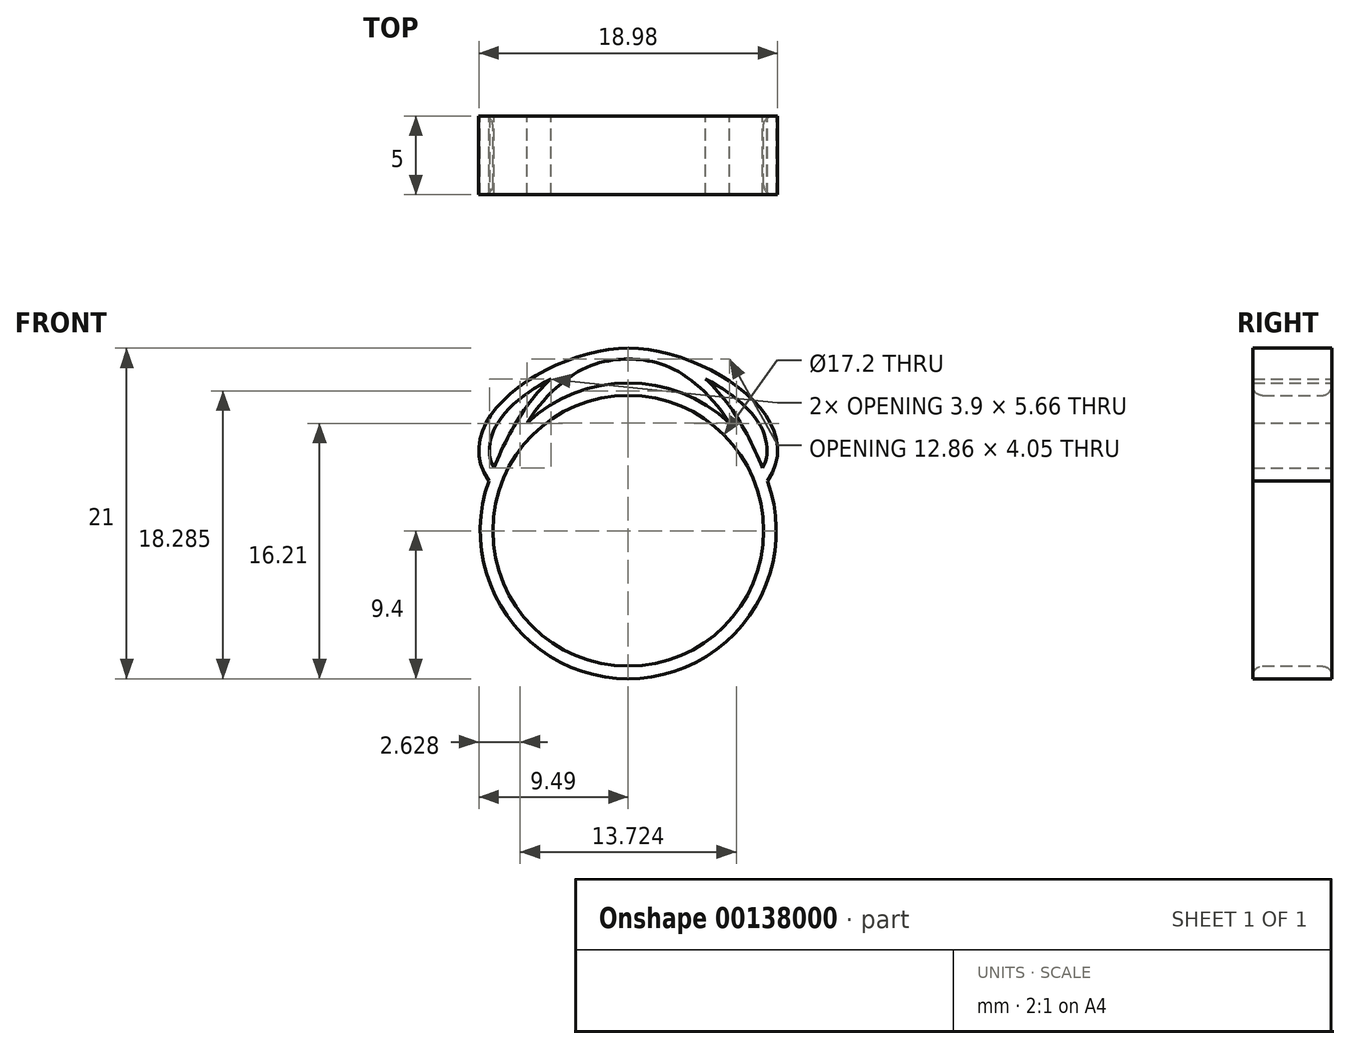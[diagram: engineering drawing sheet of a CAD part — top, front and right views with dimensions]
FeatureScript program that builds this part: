
annotation { "Feature Type Name" : "Feature", "Feature Type Description" : "" }
export const myFeature = defineFeature(function(context is Context, id is Id, definition is map)
    precondition{}
    {
        {
            var Q0;
            Q0=qCreatedBy(makeId("Front.planeOp"),FACE);
            var sketch = newSketch(context, id + "F0", { "sketchPlane" : qUnion([Q0])});
            skCircle(sketch, "E0", {"center": v(0, 0) * mm, "radius": 8.6 * mm});
            skCircle(sketch, "E1", {"center": v(0, 0) * mm, "radius": 9.4 * mm});
            skSolve(sketch);
        }
        {
            var Q0;
            Q0 = qSketchRegion(id + "F0", true);
            extrude(context, id + "F1", {"entities" : qUnion([Q0]), "depth" : 5 * mm});
        }
        {
            var Q0;
            Q0=qCreatedBy(makeId("Front.planeOp"),FACE);
            var sketch = newSketch(context, id + "F2", { "sketchPlane" : qUnion([Q0])});
            skLineSegment(sketch, "E2", {"start": v(-9.3, 3.17) * mm, "end": v(10.44, 3.17) * mm, "construction": true});
            skCircle(sketch, "E3.0", {"center": v(0, 0) * mm, "radius": 9.4 * mm, "construction": true});
            skFitSpline(sketch, "E4", {"points": [v(-8.85, 3.17) * mm, v(0, 11.6) * mm, v(8.85, 3.17) * mm], "startDerivative": vector(9, 24.34) * mm, "endDerivative": vector(-16.73, -24.34) * mm});
            skLineSegment(sketch, "E5", {"start": v(0, 3.17) * mm, "end": v(0, 13.95) * mm, "construction": true});
            skFitSpline(sketch, "E6.MirrorCS", {"points": [v(8.85, 3.17) * mm, v(0, 11.6) * mm, v(-8.85, 3.17) * mm], "startDerivative": vector(-9, 24.34) * mm, "endDerivative": vector(16.73, -24.34) * mm});
            skFitSpline(sketch, "E7.0", {"points": [v(8.2, 2.93) * mm, v(7.83, 3.92) * mm, v(6.96, 5.93) * mm, v(5.5, 8.13) * mm, v(4.08, 9.5) * mm, v(2.88, 10.27) * mm, v(1.77, 10.69) * mm, v(0.8, 10.87) * mm, v(0, 10.91) * mm, v(-0.83, 10.87) * mm, v(-2.01, 10.68) * mm, v(-3.54, 10.24) * mm, v(-5.32, 9.43) * mm, v(-6.87, 8.39) * mm, v(-8.06, 7.2) * mm, v(-8.63, 6.17) * mm, v(-8.8, 5.38) * mm, v(-8.8, 4.8) * mm, v(-8.64, 4.2) * mm, v(-8.42, 3.78) * mm, v(-8.27, 3.57) * mm]});
            skFitSpline(sketch, "E7.1", {"points": [v(-8.2, 2.93) * mm, v(-7.83, 3.92) * mm, v(-6.96, 5.93) * mm, v(-5.5, 8.13) * mm, v(-4.08, 9.5) * mm, v(-2.88, 10.27) * mm, v(-1.77, 10.69) * mm, v(-0.8, 10.87) * mm, v(0, 10.91) * mm, v(0.83, 10.87) * mm, v(2.01, 10.68) * mm, v(3.54, 10.24) * mm, v(5.32, 9.43) * mm, v(6.87, 8.39) * mm, v(8.06, 7.2) * mm, v(8.63, 6.17) * mm, v(8.8, 5.38) * mm, v(8.8, 4.8) * mm, v(8.64, 4.2) * mm, v(8.42, 3.78) * mm, v(8.27, 3.57) * mm]});
            skLineSegment(sketch, "E8", {"start": v(-8.2, 2.93) * mm, "end": v(-8.85, 3.17) * mm});
            skLineSegment(sketch, "E9", {"start": v(8.2, 2.93) * mm, "end": v(8.85, 3.17) * mm});
            skSolve(sketch);
        }
        {
            var Q0;
            Q0 = qSketchRegion(id + "F2", true);
            extrude(context, id + "F3", {"entities" : qUnion([Q0]), "operationType" : NewBodyOperationType.ADD, "depth" : 5 * mm});
        }
        {
            var Q0;
            Q0=makeQuery(id+"F1.opExtrude","CAP_EDGE",EDGE,{"disambiguationData":[OSD([sQuery(id+"F0.wireOp",EDGE,"E0")])],"isStart":false});
            var Q1;
            Q1=makeQuery(id+"F1.opExtrude","CAP_EDGE",EDGE,{"disambiguationData":[OSD([sQuery(id+"F0.wireOp",EDGE,"E0")])],"isStart":true});
            fillet(context, id + "F4", {"entities" : qUnion([Q0, Q1]), "radius" : .6 * mm, "tangentPropagation" : true, "allowEdgeOverflow" : false});
        }
    });
